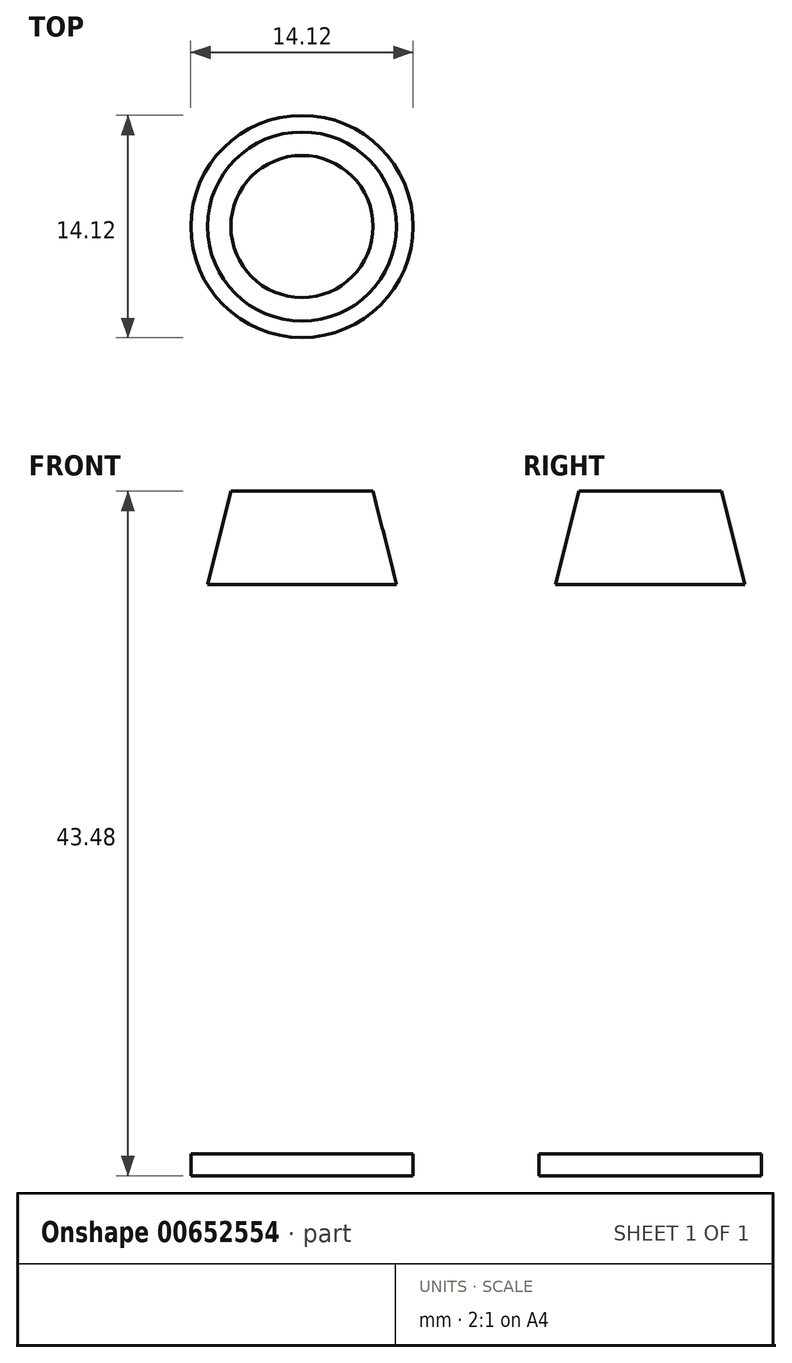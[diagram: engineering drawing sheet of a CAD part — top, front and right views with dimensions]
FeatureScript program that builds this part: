
annotation { "Feature Type Name" : "Feature", "Feature Type Description" : "" }
export const myFeature = defineFeature(function(context is Context, id is Id, definition is map)
    precondition{}
    {
        {
            var Q0;
            Q0=qCreatedBy(makeId("Top.planeOp"),FACE);
            var sketch = newSketch(context, id + "F0", { "sketchPlane" : qUnion([Q0])});
            skCircle(sketch, "E0", {"center": v(0, 0) * mm, "radius": 7.06 * mm});
            skSolve(sketch);
        }
        {
            var Q0;
            Q0=makeQuery(id+"F0.imprint","IMPRINT",FACE,{"disambiguationData":[TD([[makeQuery(id+"F0.imprint","IMPRINT",EDGE,{"derivedFrom":sQuery(id+"F0.wireOp",EDGE,"E0")}),1.0]])]});
            extrude(context, id + "F1", {"entities" : qUnion([Q0]), "depth" : 1.38 * mm, "offsetDistance" : 25.4 * mm});
        }
        {
            var Q0;
            Q0=makeQuery(id+"F1.opExtrude","CAP_FACE",FACE,{"disambiguationData":[OSD([sQuery(id+"F0.wireOp",EDGE,"E0")])],"isStart":false});
            var sketch = newSketch(context, id + "F2", { "sketchPlane" : qUnion([Q0])});
            skCircle(sketch, "E1", {"center": v(0, 0) * mm, "radius": 6.24 * mm});
            skCircle(sketch, "E2", {"center": v(0, 0) * mm, "radius": 6 * mm});
            skSolve(sketch);
        }
        {
            var Q0;
            Q0=makeQuery(id+"F2.imprint","IMPRINT",FACE,{"disambiguationData":[TD([[makeQuery(id+"F2.imprint","IMPRINT",EDGE,{"derivedFrom":sQuery(id+"F2.wireOp",EDGE,"E2")}),1.0]])]});
            cPlane(context, id + "F3", {"entities" : qUnion([Q0]), "cplaneType" : CPlaneType.OFFSET, "offset" : 36.17 * mm, "width" : 152.4 * mm, "height" : 152.4 * mm});
        }
        {
            var Q0;
            Q0=qCreatedBy(id+"F3.planeOp",FACE);
            var sketch = newSketch(context, id + "F4", { "sketchPlane" : qUnion([Q0])});
            skCircle(sketch, "E3", {"center": v(0, 0) * mm, "radius": 6 * mm});
            skSolve(sketch);
        }
        {
            var Q0;
            Q0=makeQuery(id+"F4.imprint","IMPRINT",FACE,{"disambiguationData":[TD([[makeQuery(id+"F4.imprint","IMPRINT",EDGE,{"derivedFrom":sQuery(id+"F4.wireOp",EDGE,"E3")}),1.0]])]});
            var Q1;
            Q1=sQuery(id+"F2.wireOp",EDGE,"E1");
            loft(context, id + "F5", {"bodyType" : ToolBodyType.SURFACE, "operationType" : NewBodyOperationType.INTERSECT, "wireProfilesArray" : [{ "wireProfileEntities" : qUnion([Q0]) }, { "wireProfileEntities" : qUnion([Q1]) }]});
        }
        {
            var Q0;
            Q0=qCreatedBy(id+"F3.planeOp",FACE);
            cPlane(context, id + "F6", {"entities" : qUnion([Q0]), "cplaneType" : CPlaneType.OFFSET, "offset" : 5.93 * mm, "width" : 152.4 * mm, "height" : 152.4 * mm});
        }
        {
            var Q0;
            Q0=qCreatedBy(id+"F6.planeOp",FACE);
            var sketch = newSketch(context, id + "F7", { "sketchPlane" : qUnion([Q0])});
            skCircle(sketch, "E4", {"center": v(0, 0) * mm, "radius": 4.51 * mm});
            skSolve(sketch);
        }
        {
            var Q0;
            Q0=sQuery(id+"F7.wireOp",EDGE,"E4");
            extrude(context, id + "F8", {"bodyType" : ToolBodyType.SURFACE, "surfaceEntities" : qUnion([Q0]), "depth" : 6.3 * mm, "offsetDistance" : 25.4 * mm});
        }
        {
            var Q0;
            Q0 = qSketchRegion(id + "F7", true);
            var Q1;
            Q1 = qSketchRegion(id + "F4", true);
            loft(context, id + "F9", {"sheetProfilesArray" : [{ "sheetProfileEntities" : qUnion([Q0]) }, { "sheetProfileEntities" : qUnion([Q1]) }]});
        }
    });
